FCSTD DOCUMENT  (FreeCAD 1.0R39109 (Git))
Label: 020_table_top_assembly
License: All rights reserved
LicenseURL: http://en.wikipedia.org/wiki/All_rights_reserved
objects: App::FeaturePython×17, App::Link×7, Assembly::JointGroup×1, Assembly::AssemblyObject×1
EXTERNAL_REF file=021_table_top_sheet_30mm.FCStd obj=Body
EXTERNAL_REF file=022_table_frame_front.FCStd obj=Body
EXTERNAL_REF file=023_table_frame_back.FCStd obj=Body
EXTERNAL_REF file=025_table_frame_side_left.FCStd obj=Body
EXTERNAL_REF file=026_table_frame_side_right.FCStd obj=Body
EXTERNAL_REF file=028_table_clamp.FCStd obj=Body

FEATURE [App::Link] Body
  LinkedObject = -> <external 021_table_top_sheet_30mm.FCStd>#Body
FEATURE [App::FeaturePython] GroundedJoint  # Assembly grounded joint (typed FeaturePython)
  ObjectToGround = -> Body
FEATURE [App::Link] Body001
  LinkPlacement = pos=(-4.64e-14,385,70) rot=(1,0,0;1.5708rad)
  LinkedObject = -> <external 022_table_frame_front.FCStd>#Body
  Placement = pos=(-4.64e-14,385,70) rot=(1,0,0;1.5708rad)
FEATURE [App::Link] Body002
  LinkPlacement = pos=(-2.5e-14,-385,70) rot=(0,0.707107,-0.707107;3.14159rad)
  LinkedObject = -> <external 023_table_frame_back.FCStd>#Body
  Placement = pos=(-2.5e-14,-385,70) rot=(0,0.707107,-0.707107;3.14159rad)
FEATURE [App::FeaturePython] Joint002  label="Back1"  # Assembly joint (typed FeaturePython)
  Activated = true
  AngleMax = 0
  AngleMin = 0
  Detach1 = false
  Detach2 = false
  Distance = 0
  Distance2 = 0
  EnableAngleMax = false
  EnableAngleMin = false
  EnableLengthMax = false
  EnableLengthMin = false
  JointType = 5 (Distance)
  LengthMax = 0
  LengthMin = 0
  Placement1 = pos=(1100,-6.39e-14,-4e-16) rot=(-0.57735,-0.57735,0.57735;2.0944rad)
  Placement2 = pos=(-1100,0,0) rot=(0.57735,-0.57735,0.57735;4.18879rad)
  Reference1 = -> Assembly [Body.Face3,Body.Vertex8]
  Reference2 = -> Assembly [Body002.Face1,Body002.Face1]
FEATURE [App::FeaturePython] Joint  label="Back2"  # Assembly joint (typed FeaturePython)
  Activated = true
  AngleMax = 0
  AngleMin = 0
  Detach1 = false
  Detach2 = false
  Distance = 0
  Distance2 = 0
  EnableAngleMax = false
  EnableAngleMin = false
  EnableLengthMax = false
  EnableLengthMin = false
  JointType = 5 (Distance)
  LengthMax = 0
  LengthMin = 0
  Placement1 = pos=(1.38088,55,-0.0189681) rot=(0,-0.707107,0.707107;3.14159rad)
  Placement2 = pos=(1.42e-14,-6.25e-14,15) rot=(0,0,1;0rad)
  Reference1 = -> Assembly [Body002.Face2,Body002.Vertex7]
  Reference2 = -> Assembly [Body.Face6,Body.Vertex6]
FEATURE [App::FeaturePython] Joint003  label="Back3"  # Assembly joint (typed FeaturePython)
  Activated = true
  AngleMax = 0
  AngleMin = 0
  Detach1 = false
  Detach2 = false
  Distance = 0
  Distance2 = 0
  EnableAngleMax = false
  EnableAngleMin = false
  EnableLengthMax = false
  EnableLengthMin = false
  JointType = 5 (Distance)
  LengthMax = 0
  LengthMin = 0
  Placement1 = pos=(-1010,0,15) rot=(0,0,1;0rad)
  Placement2 = pos=(-5.37e-14,-400,-4e-16) rot=(-1,0,0;1.5708rad)
  Reference1 = -> Assembly [Body002.Face5,Body002.Face5]
  Reference2 = -> Assembly [Body.Face2,Body.Vertex6]
FEATURE [App::FeaturePython] Joint004  label="Front1"  # Assembly joint (typed FeaturePython)
  Activated = true
  AngleMax = 0
  AngleMin = 0
  Detach1 = false
  Detach2 = false
  Distance = 0
  Distance2 = 0
  EnableAngleMax = false
  EnableAngleMin = false
  EnableLengthMax = false
  EnableLengthMin = false
  JointType = 5 (Distance)
  LengthMax = 0
  LengthMin = 0
  Placement1 = pos=(-3.13e-14,-55,0) rot=(-1,0,0;1.5708rad)
  Placement2 = pos=(1.42e-14,-6.25e-14,15) rot=(0,0,1;0rad)
  Reference1 = -> Assembly [Body001.Face3,Body001.Vertex4]
  Reference2 = -> Assembly [Body.Face6,Body.Vertex8]
FEATURE [App::FeaturePython] Joint005  label="Front2"  # Assembly joint (typed FeaturePython)
  Activated = true
  AngleMax = 0
  AngleMin = 0
  Detach1 = false
  Detach2 = false
  Distance = 0
  Distance2 = 0
  EnableAngleMax = false
  EnableAngleMin = false
  EnableLengthMax = false
  EnableLengthMin = false
  JointType = 5 (Distance)
  LengthMax = 0
  LengthMin = 0
  Placement1 = pos=(5.37e-14,400,-4e-16) rot=(0,-0.707107,0.707107;3.14159rad)
  Placement2 = pos=(-1.23163,0,-15) rot=(0,0,1;0rad)
  Reference1 = -> Assembly [Body.Face4,Body.Vertex7]
  Reference2 = -> Assembly [Body001.Face4,Body001.Edge5]
FEATURE [App::FeaturePython] Joint006  label="Front3"  # Assembly joint (typed FeaturePython)
  Activated = true
  AngleMax = 0
  AngleMin = 0
  Detach1 = false
  Detach2 = false
  Distance = 0
  Distance2 = 0
  EnableAngleMax = false
  EnableAngleMin = false
  EnableLengthMax = false
  EnableLengthMin = false
  JointType = 5 (Distance)
  LengthMax = 0
  LengthMin = 0
  Placement1 = pos=(1100,-6.39e-14,-4e-16) rot=(-0.57735,-0.57735,0.57735;2.0944rad)
  Placement2 = pos=(1100,0,0) rot=(-0.57735,-0.57735,0.57735;2.0944rad)
  Reference1 = -> Assembly [Body.Face3,Body.Vertex7]
  Reference2 = -> Assembly [Body001.Face6,Body001.Face6]
FEATURE [App::Link] Body003
  LinkPlacement = pos=(-1085,-1.269e-13,70) rot=(0.57735,-0.57735,0.57735;4.18879rad)
  LinkedObject = -> <external 025_table_frame_side_left.FCStd>#Body
  Placement = pos=(-1085,-1.269e-13,70) rot=(0.57735,-0.57735,0.57735;4.18879rad)
FEATURE [App::FeaturePython] Joint008  label="Left1"  # Assembly joint (typed FeaturePython)
  Activated = true
  AngleMax = 0
  AngleMin = 0
  Detach1 = false
  Detach2 = false
  Distance = 0
  Distance2 = 0
  EnableAngleMax = false
  EnableAngleMin = false
  EnableLengthMax = false
  EnableLengthMin = false
  JointType = 5 (Distance)
  LengthMax = 0
  LengthMin = 0
  Placement1 = pos=(-3.9e-15,55,0) rot=(0,-0.707107,0.707107;3.14159rad)
  Placement2 = pos=(1.42e-14,-6.25e-14,15) rot=(0,0,1;0rad)
  Reference1 = -> Assembly [Body003.Face4,Body003.Face4]
  Reference2 = -> Assembly [Body.Face6,Body.Vertex4]
FEATURE [App::FeaturePython] Joint009  label="Left2"  # Assembly joint (typed FeaturePython)
  Activated = true
  AngleMax = 0
  AngleMin = 0
  Detach1 = false
  Detach2 = false
  Distance = 0
  Distance2 = 0
  EnableAngleMax = false
  EnableAngleMin = false
  EnableLengthMax = false
  EnableLengthMin = false
  JointType = 5 (Distance)
  LengthMax = 0
  LengthMin = 0
  Placement1 = pos=(-2.1e-15,0,-15) rot=(0,0,1;0rad)
  Placement2 = pos=(-1100,-4.97e-14,-4e-16) rot=(0.57735,-0.57735,0.57735;4.18879rad)
  Reference1 = -> Assembly [Body003.Face5,Body003.Vertex7]
  Reference2 = -> Assembly [Body.Face1,Body.Face1]
FEATURE [App::FeaturePython] Joint010  label="Left3"  # Assembly joint (typed FeaturePython)
  Activated = true
  AngleMax = 0
  AngleMin = 0
  Detach1 = false
  Detach2 = false
  Distance = 0
  Distance2 = 0
  EnableAngleMax = false
  EnableAngleMin = false
  EnableLengthMax = false
  EnableLengthMin = false
  JointType = 5 (Distance)
  LengthMax = 0
  LengthMin = 0
  Placement1 = pos=(370,-1.42e-14,0) rot=(-0.57735,-0.57735,0.57735;2.0944rad)
  Placement2 = pos=(-5e-15,0,-15) rot=(0,0,1;0rad)
  Reference1 = -> Assembly [Body003.Face3,Body003.Vertex6]
  Reference2 = -> Assembly [Body002.Face4,Body002.Vertex5]
FEATURE [App::Link] Body004
  LinkPlacement = pos=(1085,-7.89e-14,70) rot=(0.57735,-0.57735,0.57735;4.18879rad)
  LinkedObject = -> <external 026_table_frame_side_right.FCStd>#Body
  Placement = pos=(1085,-7.89e-14,70) rot=(0.57735,-0.57735,0.57735;4.18879rad)
FEATURE [App::FeaturePython] Joint011  label="Right1"  # Assembly joint (typed FeaturePython)
  Activated = true
  AngleMax = 0
  AngleMin = 0
  Detach1 = false
  Detach2 = false
  Distance = 0
  Distance2 = 0
  EnableAngleMax = false
  EnableAngleMin = false
  EnableLengthMax = false
  EnableLengthMin = false
  JointType = 5 (Distance)
  LengthMax = 0
  LengthMin = 0
  Placement1 = pos=(-4.9e-15,55,0) rot=(0,0.707107,-0.707107;3.14159rad)
  Placement2 = pos=(1.42e-14,-6.25e-14,15) rot=(0,0,1;0rad)
  Reference1 = -> Assembly [Body004.Face4,Body004.Vertex2]
  Reference2 = -> Assembly [Body.Face6,Body.Vertex6]
FEATURE [App::FeaturePython] Joint012  label="Right2"  # Assembly joint (typed FeaturePython)
  Activated = true
  AngleMax = 0
  AngleMin = 0
  Detach1 = false
  Detach2 = false
  Distance = 0
  Distance2 = 0
  EnableAngleMax = false
  EnableAngleMin = false
  EnableLengthMax = false
  EnableLengthMin = false
  JointType = 5 (Distance)
  LengthMax = 0
  LengthMin = 0
  Placement1 = pos=(3.7e-15,0,15) rot=(0,0,1;0rad)
  Placement2 = pos=(1100,-6.39e-14,-4e-16) rot=(-0.57735,-0.57735,0.57735;2.0944rad)
  Reference1 = -> Assembly [Body004.Face6,Body004.Vertex2]
  Reference2 = -> Assembly [Body.Face3,Body.Face3]
FEATURE [App::FeaturePython] Joint013  label="Right3"  # Assembly joint (typed FeaturePython)
  Activated = true
  AngleMax = 0
  AngleMin = 0
  Detach1 = false
  Detach2 = false
  Distance = 0
  Distance2 = 0
  EnableAngleMax = false
  EnableAngleMin = false
  EnableLengthMax = false
  EnableLengthMin = false
  JointType = 5 (Distance)
  LengthMax = 0
  LengthMin = 0
  Placement1 = pos=(-370,0,0) rot=(-0.57735,0.57735,-0.57735;2.0944rad)
  Placement2 = pos=(-1.23163,0,15) rot=(0,0,1;0rad)
  Reference1 = -> Assembly [Body004.Face1,Body004.Face1]
  Reference2 = -> Assembly [Body001.Face5,Body001.Vertex10]
FEATURE [App::Link] Body005
  LinkPlacement = pos=(-940,548.179,55) rot=(0,-0.707107,0.707107;3.14159rad)
  LinkedObject = -> <external 028_table_clamp.FCStd>#Body
  Placement = pos=(-940,548.179,55) rot=(0,-0.707107,0.707107;3.14159rad)
FEATURE [App::FeaturePython] Joint014  label="Distance"  # Assembly joint (typed FeaturePython)
  Activated = true
  AngleMax = 0
  AngleMin = 0
  Detach1 = false
  Detach2 = false
  Distance = 0
  Distance2 = 0
  EnableAngleMax = false
  EnableAngleMin = false
  EnableLengthMax = false
  EnableLengthMin = false
  JointType = 5 (Distance)
  LengthMax = 0
  LengthMin = 0
  Placement1 = pos=(0,70,0) rot=(0,-0.707107,0.707107;3.14159rad)
  Placement2 = pos=(1.42e-14,-6.25e-14,-15) rot=(0,0,1;0rad)
  Reference1 = -> Assembly [Body005.Face4,Body005.Face4]
  Reference2 = -> Assembly [Body.Face5,Body.Vertex1]
FEATURE [App::FeaturePython] Joint015  label="Distance001"  # Assembly joint (typed FeaturePython)
  Activated = true
  AngleMax = 0
  AngleMin = 0
  Detach1 = false
  Detach2 = false
  Distance = 0
  Distance2 = 0
  EnableAngleMax = false
  EnableAngleMin = false
  EnableLengthMax = false
  EnableLengthMin = false
  JointType = 5 (Distance)
  LengthMax = 0
  LengthMin = 0
  Placement1 = pos=(-1100,0,0) rot=(-0.57735,0.57735,-0.57735;2.0944rad)
  Placement2 = pos=(160,0,0) rot=(-0.57735,-0.57735,0.57735;2.0944rad)
  Reference1 = -> Assembly [Body001.Face1,Body001.Vertex4]
  Reference2 = -> Assembly [Body005.Face3,Body005.Face3]
FEATURE [App::Link] Body006
  LinkPlacement = pos=(1255.62,240,55) rot=(-0.57735,-0.57735,0.57735;2.0944rad)
  LinkedObject = -> <external 028_table_clamp.FCStd>#Body
  Placement = pos=(1255.62,240,55) rot=(-0.57735,-0.57735,0.57735;2.0944rad)
FEATURE [App::FeaturePython] Joint016  label="Distance002"  # Assembly joint (typed FeaturePython)
  Activated = true
  AngleMax = 0
  AngleMin = 0
  Detach1 = false
  Detach2 = false
  Distance = 0
  Distance2 = 0
  EnableAngleMax = false
  EnableAngleMin = false
  EnableLengthMax = false
  EnableLengthMin = false
  JointType = 5 (Distance)
  LengthMax = 0
  LengthMin = 0
  Placement1 = pos=(160,0,0) rot=(-0.57735,-0.57735,0.57735;2.0944rad)
  Placement2 = pos=(-1.23163,0,-15) rot=(0,0,1;0rad)
  Reference1 = -> Assembly [Body006.Face3,Body006.Vertex8]
  Reference2 = -> Assembly [Body001.Face4,Body001.Edge5]
FEATURE [App::FeaturePython] Joint017  label="Distance003"  # Assembly joint (typed FeaturePython)
  Activated = true
  AngleMax = 0
  AngleMin = 0
  Detach1 = false
  Detach2 = false
  Distance = 0
  Distance2 = 0
  EnableAngleMax = false
  EnableAngleMin = false
  EnableLengthMax = false
  EnableLengthMin = false
  JointType = 5 (Distance)
  LengthMax = 0
  LengthMin = 0
  Placement1 = pos=(0,70,0) rot=(0,-0.707107,0.707107;3.14159rad)
  Placement2 = pos=(1.42e-14,-6.25e-14,-15) rot=(0,0,1;0rad)
  Reference1 = -> Assembly [Body006.Face4,Body006.Face4]
  Reference2 = -> Assembly [Body.Face5,Body.Vertex7]
FEATURE [Assembly::JointGroup] Joints
  Group = -> [GroundedJoint,Joint002,Joint,Joint003,Joint004,Joint005,Joint006,Joint008,Joint009,Joint010,Joint011,Joint012,Joint013,Joint014,Joint015,Joint016,Joint017]
FEATURE [Assembly::AssemblyObject] Assembly
  Group = -> [Joints,Body,GroundedJoint,Body001,Body002,Joint002,Joint,Joint003,Joint004,Joint005,Joint006,Body003,Joint008,Joint009,Joint010,Body004,Joint011,Joint012,Joint013,Body005,Joint014,Joint015,Body006,Joint016,Joint017]
  Origin = -> Origin
  Type = Assembly

RESOLVED EXTERNAL PARTS (link-assembly join: the EXTERNAL_REF files above that resolve inside this repo's crawl, each included once):
---- part 021_table_top_sheet_30mm.FCStd = doc fcstd_82890d6540b6 ----
FCSTD DOCUMENT  (FreeCAD 1.0R39109 (Git))
Label: 021_top_sheet_30mm
License: All rights reserved
LicenseURL: http://en.wikipedia.org/wiki/All_rights_reserved
objects: Spreadsheet::Sheet×1, Sketcher::SketchObject×1, PartDesign::Pad×1, PartDesign::Body×1
note: 6 computed .brp shape members not serialized (recipe doc carries the construction recipe); baked Part::Feature solids carry a one-line shape summary decoded from their .brp

FEATURE [Spreadsheet::Sheet] Spreadsheet
  cells = A4='length; B4(length)=2200; A5='width; B5(width)=800; A6='height; B6(height)=30
FEATURE [Sketcher::SketchObject] Sketch
  ArcFitTolerance = 1e-06
  AttachmentSupport = -> [XY_Plane]
  FullyConstrained = true
  MakeInternals = false
  MapMode = 5
  expr: Constraints[11] = Spreadsheet.length
  expr: Constraints[12] = Spreadsheet.width
  sketch-geometry (5):
    g0: LineSegment StartX=-1100 StartY=400 StartZ=0 EndX=-1100 EndY=-400 EndZ=0
    g1: LineSegment StartX=-1100 StartY=-400 StartZ=0 EndX=1100 EndY=-400 EndZ=0
    g2: LineSegment StartX=1100 StartY=-400 StartZ=0 EndX=1100 EndY=400 EndZ=0
    g3: LineSegment StartX=1100 StartY=400 StartZ=0 EndX=-1100 EndY=400 EndZ=0
    g4: LineSegment [constr] StartX=-1100 StartY=400 StartZ=0 EndX=1100 EndY=-400 EndZ=0
  constraints (13):
    c: Coincident(g0,g1)
    c: Coincident(g1,g2)
    c: Coincident(g2,g3)
    c: Coincident(g3,g0)
    c: Vertical(g0)
    c: Vertical(g2)
    c: Horizontal(g1)
    c: Horizontal(g3)
    c: Coincident(g4,g0)
    c: Coincident(g4,g1)
    c: Symmetric(g4,g4,g-1)
    c: DistanceX(g3,g3) = 2200
    c: DistanceY(g0,g0) = 800
FEATURE [PartDesign::Pad] Pad
  Direction = (0,0,1)
  Length = 30
  Length2 = 10
  Midplane = true
  Profile = -> Sketch
  ReferenceAxis = -> Sketch [N_Axis]
  Suppressed = false
  Type = 0
  expr: Length = Spreadsheet.height
FEATURE [PartDesign::Body] Body
  AllowCompound = false
  Group = -> [Sketch,Pad]
  Origin = -> Origin
  Tip = -> Pad
---- part 022_table_frame_front.FCStd = doc fcstd_3d8f9efe90f7 ----
FCSTD DOCUMENT  (FreeCAD 1.0R39109 (Git))
Label: 022_table_frame_front
License: All rights reserved
LicenseURL: http://en.wikipedia.org/wiki/All_rights_reserved
objects: Sketcher::SketchObject×2, Spreadsheet::Sheet×1, PartDesign::Pad×1, PartDesign::Pocket×1, PartDesign::Body×1
note: 11 computed .brp shape members not serialized (recipe doc carries the construction recipe); baked Part::Feature solids carry a one-line shape summary decoded from their .brp

FEATURE [Spreadsheet::Sheet] Spreadsheet
  cells = A4='length; B4(length)=2200; A5='width; B5(width)=110; A6='height; B6(height)=30
FEATURE [Sketcher::SketchObject] Sketch
  ArcFitTolerance = 1e-06
  AttachmentSupport = -> [XY_Plane]
  FullyConstrained = true
  MakeInternals = false
  MapMode = 5
  expr: Constraints[11] = Spreadsheet.length
  expr: Constraints[12] = Spreadsheet.width
  sketch-geometry (5):
    g0: LineSegment StartX=-1100 StartY=55 StartZ=0 EndX=-1100 EndY=-55 EndZ=0
    g1: LineSegment StartX=-1100 StartY=-55 StartZ=0 EndX=1100 EndY=-55 EndZ=0
    g2: LineSegment StartX=1100 StartY=-55 StartZ=0 EndX=1100 EndY=55 EndZ=0
    g3: LineSegment StartX=1100 StartY=55 StartZ=0 EndX=-1100 EndY=55 EndZ=0
    g4: LineSegment [constr] StartX=-1100 StartY=55 StartZ=0 EndX=1100 EndY=-55 EndZ=0
  constraints (13):
    c: Coincident(g0,g1)
    c: Coincident(g1,g2)
    c: Coincident(g2,g3)
    c: Coincident(g3,g0)
    c: Vertical(g0)
    c: Vertical(g2)
    c: Horizontal(g1)
    c: Horizontal(g3)
    c: Coincident(g4,g0)
    c: Coincident(g4,g1)
    c: Symmetric(g4,g4,g-1)
    c: DistanceX(g3,g3) = 2200
    c: DistanceY(g0,g0) = 110
FEATURE [PartDesign::Pad] Pad
  Direction = (0,0,1)
  Length = 30
  Length2 = 10
  Midplane = true
  Profile = -> Sketch
  ReferenceAxis = -> Sketch [N_Axis]
  Suppressed = false
  Type = 0
  expr: Length = Spreadsheet.height
FEATURE [Sketcher::SketchObject] Sketch001
  ArcFitTolerance = 1e-06
  AttachmentSupport = -> [XY_Plane]
  ExternalGeometry = -> [Pad]
  FullyConstrained = true
  MakeInternals = false
  MapMode = 5
  sketch-geometry (2):
    g0: LineSegment [constr] StartX=-1100 StartY=0 StartZ=0 EndX=1100 EndY=0 EndZ=0
    g1: Circle CenterX=1050 CenterY=0 CenterZ=0 NormalX=0 NormalY=0 NormalZ=1 AngleXU=0 Radius=9.5
  constraints (5):
    c: Symmetric(g-3,g-3,g0)
    c: Symmetric(g-4,g-4,g0)
    c: PointOnObject(g1,g0)
    c: Diameter(g1) = 19
    c: Distance(g1,g-4) = 50
FEATURE [PartDesign::Pocket] Pocket
  BaseFeature = -> Pad
  Direction = (0,0,-1)
  Length = 5
  Length2 = 5
  Midplane = true
  Profile = -> Sketch001
  ReferenceAxis = -> Sketch001 [N_Axis]
  Suppressed = false
  Type = 1
FEATURE [PartDesign::Body] Body
  AllowCompound = false
  Group = -> [Sketch,Pad,Sketch001,Pocket]
  Origin = -> Origin
  Tip = -> Pocket
---- part 023_table_frame_back.FCStd = doc fcstd_7a45e0af9c49 ----
FCSTD DOCUMENT  (FreeCAD 1.0R39109 (Git))
Label: 023_table_frame_back
License: All rights reserved
LicenseURL: http://en.wikipedia.org/wiki/All_rights_reserved
objects: Sketcher::SketchObject×2, Spreadsheet::Sheet×1, PartDesign::Pad×1, PartDesign::Pocket×1, PartDesign::Body×1
note: 11 computed .brp shape members not serialized (recipe doc carries the construction recipe); baked Part::Feature solids carry a one-line shape summary decoded from their .brp

FEATURE [Spreadsheet::Sheet] Spreadsheet
  cells = A4='length; B4(length)=2200; A5='width; B5(width)=110; A6='height; B6(height)=30
FEATURE [Sketcher::SketchObject] Sketch
  ArcFitTolerance = 1e-06
  AttachmentSupport = -> [XY_Plane]
  FullyConstrained = true
  MakeInternals = false
  MapMode = 5
  expr: Constraints[11] = Spreadsheet.length
  expr: Constraints[12] = Spreadsheet.width
  sketch-geometry (5):
    g0: LineSegment StartX=-1100 StartY=55 StartZ=0 EndX=-1100 EndY=-55 EndZ=0
    g1: LineSegment StartX=-1100 StartY=-55 StartZ=0 EndX=1100 EndY=-55 EndZ=0
    g2: LineSegment StartX=1100 StartY=-55 StartZ=0 EndX=1100 EndY=55 EndZ=0
    g3: LineSegment StartX=1100 StartY=55 StartZ=0 EndX=-1100 EndY=55 EndZ=0
    g4: LineSegment [constr] StartX=-1100 StartY=55 StartZ=0 EndX=1100 EndY=-55 EndZ=0
  constraints (13):
    c: Coincident(g0,g1)
    c: Coincident(g1,g2)
    c: Coincident(g2,g3)
    c: Coincident(g3,g0)
    c: Vertical(g0)
    c: Vertical(g2)
    c: Horizontal(g1)
    c: Horizontal(g3)
    c: Coincident(g4,g0)
    c: Coincident(g4,g1)
    c: Symmetric(g4,g4,g-1)
    c: DistanceX(g3,g3) = 2200
    c: DistanceY(g0,g0) = 110
FEATURE [PartDesign::Pad] Pad
  Direction = (0,0,1)
  Length = 30
  Length2 = 10
  Midplane = true
  Profile = -> Sketch
  ReferenceAxis = -> Sketch [N_Axis]
  Suppressed = false
  Type = 0
  expr: Length = Spreadsheet.height
FEATURE [Sketcher::SketchObject] Sketch001
  ArcFitTolerance = 1e-06
  AttachmentOffset = pos=(0,0,15) rot=(0,0,1;0rad)
  AttachmentSupport = -> [XY_Plane]
  ExternalGeometry = -> [Pad]
  FullyConstrained = true
  MakeInternals = false
  MapMode = 5
  Placement = pos=(0,0,15) rot=(0,0,1;0rad)
  expr: .AttachmentOffset.Base.z = Spreadsheet.height / 2
  sketch-geometry (6):
    g0: LineSegment [constr] StartX=-1100 StartY=0 StartZ=0 EndX=1100 EndY=0 EndZ=0
    g1: LineSegment StartX=-900 StartY=55 StartZ=0 EndX=-900 EndY=-55 EndZ=0
    g2: LineSegment StartX=-900 StartY=-55 StartZ=0 EndX=-920 EndY=-55 EndZ=0
    g3: LineSegment StartX=-920 StartY=-55 StartZ=0 EndX=-920 EndY=55 EndZ=0
    g4: LineSegment StartX=-920 StartY=55 StartZ=0 EndX=-900 EndY=55 EndZ=0
    g5: LineSegment [constr] StartX=-910 StartY=55 StartZ=0 EndX=-910 EndY=-55 EndZ=0
  constraints (18):
    c: Symmetric(g-3,g-3,g0)
    c: PointOnObject(g0,g-4)
    c: Horizontal(g0)
    c: Coincident(g1,g2)
    c: Coincident(g2,g3)
    c: Coincident(g3,g4)
    c: Coincident(g4,g1)
    c: Vertical(g1)
    c: Vertical(g3)
    c: Horizontal(g2)
    c: Horizontal(g4)
    c: PointOnObject(g1,g-5)
    c: PointOnObject(g2,g-6)
    c: PointOnObject(g5,g4)
    c: Symmetric(g2,g2,g5)
    c: Vertical(g5)
    c: Distance(g4,g4) = 20
    c: DistanceX(g-5,g1) = 200
FEATURE [PartDesign::Pocket] Pocket
  BaseFeature = -> Pad
  Direction = (0,0,-1)
  Length = 5
  Length2 = 5
  Profile = -> Sketch001
  ReferenceAxis = -> Sketch001 [N_Axis]
  Suppressed = false
  Type = 0
FEATURE [PartDesign::Body] Body
  AllowCompound = false
  Group = -> [Sketch,Pad,Sketch001,Pocket]
  Origin = -> Origin
  Tip = -> Pocket
---- part 025_table_frame_side_left.FCStd = doc fcstd_d9bef339f21d ----
FCSTD DOCUMENT  (FreeCAD 1.0R39109 (Git))
Label: 025_table_frame_side_left
License: All rights reserved
LicenseURL: http://en.wikipedia.org/wiki/All_rights_reserved
objects: Spreadsheet::Sheet×1, Sketcher::SketchObject×1, PartDesign::Pad×1, PartDesign::Body×1
note: 6 computed .brp shape members not serialized (recipe doc carries the construction recipe); baked Part::Feature solids carry a one-line shape summary decoded from their .brp

FEATURE [Spreadsheet::Sheet] Spreadsheet
  cells = A4='length; B4(length)=800; A5='width; B5(width)=110; A6='height; B6(height)=30
FEATURE [Sketcher::SketchObject] Sketch
  ArcFitTolerance = 1e-06
  AttachmentSupport = -> [XY_Plane]
  FullyConstrained = true
  MakeInternals = false
  MapMode = 5
  expr: Constraints[11] = Spreadsheet.length - 2 * Spreadsheet.height
  expr: Constraints[12] = Spreadsheet.width
  sketch-geometry (5):
    g0: LineSegment StartX=-370 StartY=55 StartZ=0 EndX=-370 EndY=-55 EndZ=0
    g1: LineSegment StartX=-370 StartY=-55 StartZ=0 EndX=370 EndY=-55 EndZ=0
    g2: LineSegment StartX=370 StartY=-55 StartZ=0 EndX=370 EndY=55 EndZ=0
    g3: LineSegment StartX=370 StartY=55 StartZ=0 EndX=-370 EndY=55 EndZ=0
    g4: LineSegment [constr] StartX=-370 StartY=55 StartZ=0 EndX=370 EndY=-55 EndZ=0
  constraints (13):
    c: Coincident(g0,g1)
    c: Coincident(g1,g2)
    c: Coincident(g2,g3)
    c: Coincident(g3,g0)
    c: Vertical(g0)
    c: Vertical(g2)
    c: Horizontal(g1)
    c: Horizontal(g3)
    c: Coincident(g4,g0)
    c: Coincident(g4,g1)
    c: Symmetric(g4,g4,g-1)
    c: DistanceX(g3,g3) = 740
    c: DistanceY(g0,g0) = 110
FEATURE [PartDesign::Pad] Pad
  Direction = (0,0,1)
  Length = 30
  Length2 = 10
  Midplane = true
  Profile = -> Sketch
  ReferenceAxis = -> Sketch [N_Axis]
  Suppressed = false
  Type = 0
  expr: Length = Spreadsheet.height
FEATURE [PartDesign::Body] Body
  AllowCompound = false
  Group = -> [Sketch,Pad]
  Origin = -> Origin
  Tip = -> Pad
---- part 026_table_frame_side_right.FCStd = doc fcstd_2c3fbff15b88 ----
FCSTD DOCUMENT  (FreeCAD 1.0R39109 (Git))
Label: 025_table_frame_side_right
License: All rights reserved
LicenseURL: http://en.wikipedia.org/wiki/All_rights_reserved
objects: Spreadsheet::Sheet×1, Sketcher::SketchObject×1, PartDesign::Pad×1, PartDesign::Body×1
note: 6 computed .brp shape members not serialized (recipe doc carries the construction recipe); baked Part::Feature solids carry a one-line shape summary decoded from their .brp

FEATURE [Spreadsheet::Sheet] Spreadsheet
  cells = A4='length; B4(length)=800; A5='width; B5(width)=110; A6='height; B6(height)=30
FEATURE [Sketcher::SketchObject] Sketch
  ArcFitTolerance = 1e-06
  AttachmentSupport = -> [XY_Plane]
  FullyConstrained = true
  MakeInternals = false
  MapMode = 5
  expr: Constraints[11] = Spreadsheet.length - 2 * Spreadsheet.height
  expr: Constraints[12] = Spreadsheet.width
  sketch-geometry (5):
    g0: LineSegment StartX=-370 StartY=55 StartZ=0 EndX=-370 EndY=-55 EndZ=0
    g1: LineSegment StartX=-370 StartY=-55 StartZ=0 EndX=370 EndY=-55 EndZ=0
    g2: LineSegment StartX=370 StartY=-55 StartZ=0 EndX=370 EndY=55 EndZ=0
    g3: LineSegment StartX=370 StartY=55 StartZ=0 EndX=-370 EndY=55 EndZ=0
    g4: LineSegment [constr] StartX=-370 StartY=55 StartZ=0 EndX=370 EndY=-55 EndZ=0
  constraints (13):
    c: Coincident(g0,g1)
    c: Coincident(g1,g2)
    c: Coincident(g2,g3)
    c: Coincident(g3,g0)
    c: Vertical(g0)
    c: Vertical(g2)
    c: Horizontal(g1)
    c: Horizontal(g3)
    c: Coincident(g4,g0)
    c: Coincident(g4,g1)
    c: Symmetric(g4,g4,g-1)
    c: DistanceX(g3,g3) = 740
    c: DistanceY(g0,g0) = 110
FEATURE [PartDesign::Pad] Pad
  Direction = (0,0,1)
  Length = 30
  Length2 = 10
  Midplane = true
  Profile = -> Sketch
  ReferenceAxis = -> Sketch [N_Axis]
  Suppressed = false
  Type = 0
  expr: Length = Spreadsheet.height
FEATURE [PartDesign::Body] Body
  AllowCompound = false
  Group = -> [Sketch,Pad]
  Origin = -> Origin
  Tip = -> Pad
---- part 028_table_clamp.FCStd = doc fcstd_9e36eed2fe1d ----
FCSTD DOCUMENT  (FreeCAD 1.0R39109 (Git))
Label: 028_table_clamp
License: All rights reserved
LicenseURL: http://en.wikipedia.org/wiki/All_rights_reserved
objects: Spreadsheet::Sheet×1, Sketcher::SketchObject×1, PartDesign::Pad×1, PartDesign::Body×1
note: 6 computed .brp shape members not serialized (recipe doc carries the construction recipe); baked Part::Feature solids carry a one-line shape summary decoded from their .brp

FEATURE [Spreadsheet::Sheet] Spreadsheet
  cells = A4='length; B4(length)=500; A5='width; B5(width)=140; A6='height; B6(height)=90
FEATURE [Sketcher::SketchObject] Sketch
  ArcFitTolerance = 1e-06
  AttachmentSupport = -> [XY_Plane]
  FullyConstrained = true
  MakeInternals = false
  MapMode = 5
  expr: Constraints[11] = Spreadsheet.length - 2 * Spreadsheet.height
  expr: Constraints[12] = Spreadsheet.width
  sketch-geometry (5):
    g0: LineSegment StartX=-160 StartY=70 StartZ=0 EndX=-160 EndY=-70 EndZ=0
    g1: LineSegment StartX=-160 StartY=-70 StartZ=0 EndX=160 EndY=-70 EndZ=0
    g2: LineSegment StartX=160 StartY=-70 StartZ=0 EndX=160 EndY=70 EndZ=0
    g3: LineSegment StartX=160 StartY=70 StartZ=0 EndX=-160 EndY=70 EndZ=0
    g4: LineSegment [constr] StartX=-160 StartY=70 StartZ=0 EndX=160 EndY=-70 EndZ=0
  constraints (13):
    c: Coincident(g0,g1)
    c: Coincident(g1,g2)
    c: Coincident(g2,g3)
    c: Coincident(g3,g0)
    c: Vertical(g0)
    c: Vertical(g2)
    c: Horizontal(g1)
    c: Horizontal(g3)
    c: Coincident(g4,g0)
    c: Coincident(g4,g1)
    c: Symmetric(g4,g4,g-1)
    c: DistanceX(g3,g3) = 320
    c: DistanceY(g0,g0) = 140
FEATURE [PartDesign::Pad] Pad
  Direction = (0,0,1)
  Length = 90
  Length2 = 10
  Midplane = true
  Profile = -> Sketch
  ReferenceAxis = -> Sketch [N_Axis]
  Suppressed = false
  Type = 0
  expr: Length = Spreadsheet.height
FEATURE [PartDesign::Body] Body
  AllowCompound = false
  Group = -> [Sketch,Pad]
  Origin = -> Origin
  Tip = -> Pad
